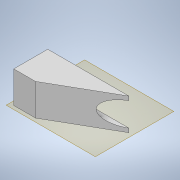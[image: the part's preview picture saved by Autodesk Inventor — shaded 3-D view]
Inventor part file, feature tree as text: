
AUTODESK INVENTOR PART (.ipt)
format: ipt  version: 2022.3 (Build 263350000, 350)  size: 115,712 bytes
history: native  units: mm
features: extrude x3, sketch x3, other x2, plane x1, reference x1
ambient origin geometry x8: Origin, YZ Plane, XZ Plane, XY Plane, X Axis, Y Axis, Z Axis, Center Point
bodies: Solid1 (feature_tree)
feature tree (10):
  plane  "Work Plane1"
  extrude  "Extrusion1"  Depth=8.0mm
  extrude  "Extrusion2"  TaperAngle=0.0deg  [1 undecoded]
  extrude  "Extrusion3"  [1 undecoded]
  sketch  "Sketch1"  dims[d0=8.0mm d1=0.0mm d2=6.0mm]
  reference  "Reference1"
  sketch  "Sketch2"  dims[d3=15.981mm d4=0.0mm d9=0.0mm d10=0.0mm]
  sketch  "Sketch3"
  other  "v2.0.iam"
  other  "Base:1"
note: 2 required parameter values undecoded (feature->parameter linkage not recoverable at this tier; creation-order binding heuristic only, values carry confidence <= 0.55)
